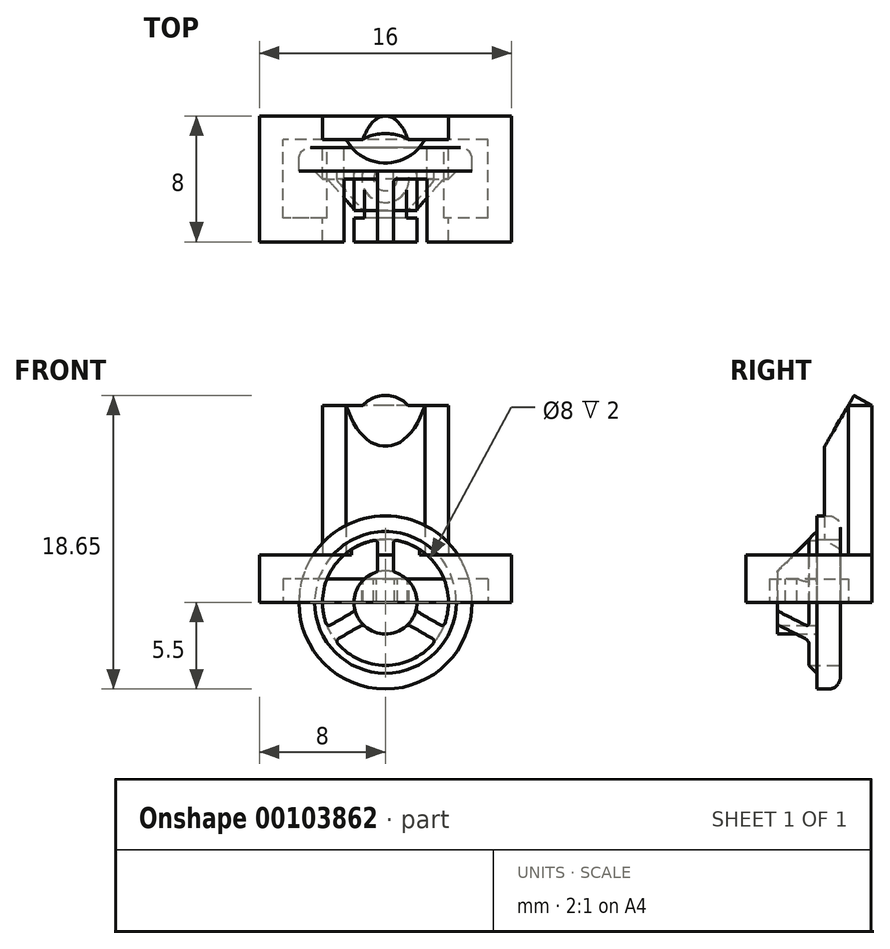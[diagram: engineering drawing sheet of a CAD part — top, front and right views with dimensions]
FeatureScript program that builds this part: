
annotation { "Feature Type Name" : "Feature", "Feature Type Description" : "" }
export const myFeature = defineFeature(function(context is Context, id is Id, definition is map)
    precondition{}
    {
        {
            var Q0;
            Q0=qCreatedBy(makeId("Top.planeOp"),FACE);
            var sketch = newSketch(context, id + "F0", { "sketchPlane" : qUnion([Q0])});
            skLineSegment(sketch, "E0.bottom", {"start": v(8, -4) * mm, "end": v(-8, -4) * mm});
            skLineSegment(sketch, "E0.top", {"start": v(8, 4) * mm, "end": v(-8, 4) * mm});
            skLineSegment(sketch, "E0.left", {"start": v(8, -4) * mm, "end": v(8, 4) * mm});
            skLineSegment(sketch, "E0.right", {"start": v(-8, -4) * mm, "end": v(-8, 4) * mm});
            skPoint(sketch, "E0.middle", {"position": v(0, 0) * mm});
            skSolve(sketch);
        }
        {
            var Q0;
            Q0=makeQuery(id+"F0.imprint","IMPRINT",FACE,{"disambiguationData":[TD([[makeQuery(id+"F0.imprint","IMPRINT",EDGE,{"derivedFrom":sQuery(id+"F0.wireOp",EDGE,"E0.bottom")}),-1.0]])]});
            extrude(context, id + "F1", {"entities" : qUnion([Q0]), "depth" : 3 * mm});
        }
        {
            var Q0;
            Q0=makeQuery(id+"F1.opExtrude","CAP_FACE",FACE,{"disambiguationData":[OSD([sQuery(id+"F0.wireOp",EDGE,"E0.bottom"),sQuery(id+"F0.wireOp",EDGE,"E0.top"),sQuery(id+"F0.wireOp",EDGE,"E0.left"),sQuery(id+"F0.wireOp",EDGE,"E0.right")])],"isStart":true});
            shell(context, id + "F2", {"entities" : qUnion([Q0]), "thickness" : 1.5 * mm});
        }
        {
            var Q0;
            Q0=makeQuery(id+"F2.opShell","OFFSET_FACE",FACE,{"disambiguationData":[OSD([sQuery(id+"F0.wireOp",EDGE,"E0.bottom"),sQuery(id+"F0.wireOp",EDGE,"E0.top"),sQuery(id+"F0.wireOp",EDGE,"E0.left"),sQuery(id+"F0.wireOp",EDGE,"E0.right")])]});
            var sketch = newSketch(context, id + "F3", { "sketchPlane" : qUnion([Q0])});
            skCircle(sketch, "E1", {"center": v(0, 0) * mm, "radius": 1.5 * mm});
            skCircle(sketch, "E2.0", {"center": v(0, 0) * mm, "radius": 0.75 * mm});
            skSolve(sketch);
        }
        {
            var Q0;
            Q0=makeQuery(id+"F3.imprint","IMPRINT",FACE,{"disambiguationData":[TD([[makeQuery(id+"F3.imprint","IMPRINT",EDGE,{"derivedFrom":sQuery(id+"F3.wireOp",EDGE,"E1")}),1.0]])]});
            var Q1;
            Q1=makeQuery(id+"F1.opExtrude","CAP_FACE",FACE,{"disambiguationData":[OSD([sQuery(id+"F0.wireOp",EDGE,"E0.bottom"),sQuery(id+"F0.wireOp",EDGE,"E0.top"),sQuery(id+"F0.wireOp",EDGE,"E0.left"),sQuery(id+"F0.wireOp",EDGE,"E0.right")])],"isStart":true});
            extrude(context, id + "F4", {"entities" : qUnion([Q0]), "operationType" : NewBodyOperationType.ADD, "endBound" : BoundingType.UP_TO_SURFACE, "endBoundEntityFace" : qUnion([Q1]), "depth" : 25 * mm});
        }
        {
            var Q0;
            Q0=makeQuery(id+"F1.opExtrude","CAP_FACE",FACE,{"disambiguationData":[OSD([sQuery(id+"F0.wireOp",EDGE,"E0.bottom"),sQuery(id+"F0.wireOp",EDGE,"E0.top"),sQuery(id+"F0.wireOp",EDGE,"E0.left"),sQuery(id+"F0.wireOp",EDGE,"E0.right")])],"isStart":false});
            var sketch = newSketch(context, id + "F5", { "sketchPlane" : qUnion([Q0])});
            skLineSegment(sketch, "E3", {"start": v(0, 4) * mm, "end": v(0, -4) * mm, "construction": true});
            skLineSegment(sketch, "E4.bottom", {"start": v(-4, 4) * mm, "end": v(4, 4) * mm});
            skLineSegment(sketch, "E4.top", {"start": v(-4, 2.5) * mm, "end": v(-2.5, 2.5) * mm});
            skLineSegment(sketch, "E4.left", {"start": v(-4, 4) * mm, "end": v(-4, 2.5) * mm});
            skLineSegment(sketch, "E4.right", {"start": v(4, 4) * mm, "end": v(4, 2.5) * mm});
            skArc(sketch, "E5", {"start": v(-2.5, 2.5) * mm, "mid": v(0, 1) * mm, "end": v(2.5, 2.5) * mm});
            skLineSegment(sketch, "E6.0", {"start": v(-4, 1) * mm, "end": v(4, 1) * mm, "construction": true});
            skLineSegment(sketch, "E7.trimOffspring", {"start": v(2.5, 2.5) * mm, "end": v(4, 2.5) * mm});
            skSolve(sketch);
        }
        {
            var Q0;
            Q0=makeQuery(id+"F5.imprint","IMPRINT",FACE,{"disambiguationData":[TD([[makeQuery(id+"F5.imprint","IMPRINT",EDGE,{"derivedFrom":sQuery(id+"F5.wireOp",EDGE,"E4.bottom")}),1.0]])]});
            extrude(context, id + "F6", {"entities" : qUnion([Q0]), "operationType" : NewBodyOperationType.ADD, "depth" : 9.5 * mm});
        }
        {
            var Q0;
            Q0=makeQuery(id+"F6.opExtrude","SWEPT_FACE",FACE,{"disambiguationData":[OSD([sQuery(id+"F5.wireOp",EDGE,"E4.left")])]});
            var sketch = newSketch(context, id + "F7", { "sketchPlane" : qUnion([Q0])});
            skLineSegment(sketch, "E8", {"start": v(-2.5, 12.5) * mm, "end": v(0.42, 12.5) * mm});
            skLineSegment(sketch, "E9", {"start": v(0.42, 12.5) * mm, "end": v(0.42, 7.44) * mm});
            skLineSegment(sketch, "E10", {"start": v(0.42, 7.44) * mm, "end": v(-2.5, 12.5) * mm});
            skSolve(sketch);
        }
        {
            var Q0;
            Q0=makeQuery(id+"F7.imprint","IMPRINT",FACE,{"disambiguationData":[TD([[makeQuery(id+"F7.imprint","IMPRINT",EDGE,{"derivedFrom":sQuery(id+"F7.wireOp",EDGE,"E8")}),-1.0]])]});
            extrude(context, id + "F8", {"entities" : qUnion([Q0]), "operationType" : NewBodyOperationType.REMOVE, "endBound" : BoundingType.THROUGH_ALL, "oppositeDirection" : true, "depth" : 25 * mm});
        }
        {
            var Q0;
            Q0=qCreatedBy(makeId("Right.planeOp"),FACE);
            var sketch = newSketch(context, id + "F9", { "sketchPlane" : qUnion([Q0])});
            skLineSegment(sketch, "E11", {"start": v(-2, 0) * mm, "end": v(-2, 2) * mm});
            skLineSegment(sketch, "E12", {"start": v(-2, 2) * mm, "end": v(0.5, 4.5) * mm});
            skLineSegment(sketch, "E13", {"start": v(0.5, 4.5) * mm, "end": v(0.5, 5.5) * mm});
            skLineSegment(sketch, "E14", {"start": v(0.5, 5.5) * mm, "end": v(2, 5.5) * mm});
            skLineSegment(sketch, "E15", {"start": v(2, 0) * mm, "end": v(-2, 0) * mm});
            skPoint(sketch, "E16.orphan", {"position": v(2.44, 0) * mm});
            skLineSegment(sketch, "E17", {"start": v(2, 5.5) * mm, "end": v(2, 0) * mm});
            skSolve(sketch);
        }
        {
            var Q0;
            Q0 = qSketchRegion(id + "F9", true);
            var Q1;
            Q1=sQuery(id+"F9.wireOp",EDGE,"E15");
            revolve(context, id + "F10", {"entities" : qUnion([Q0]), "axis" : qUnion([Q1]), "revolveType" : RevolveType.FULL});
        }
        {
            var Q0;
            Q0=makeQuery(id+"F10.opRevolve","SWEPT_FACE",FACE,{"disambiguationData":[OSD([sQuery(id+"F9.wireOp",EDGE,"E17")])]});
            var sketch = newSketch(context, id + "F11", { "sketchPlane" : qUnion([Q0])});
            skArc(sketch, "E18", {"start": v(3.77, -1.33) * mm, "mid": v(3.46, 2) * mm, "end": v(0.74, 3.93) * mm});
            skArc(sketch, "E19", {"start": v(1.96, -0.4) * mm, "mid": v(1.73, 1) * mm, "end": v(0.64, 1.9) * mm});
            skLineSegment(sketch, "E20.0", {"start": v(0.5, 3.73) * mm, "end": v(0.5, 2.09) * mm});
            skLineSegment(sketch, "E21", {"start": v(0, 6.2) * mm, "end": v(0, -6.27) * mm, "construction": true});
            skLineSegment(sketch, "E22.1.1", {"start": v(3.48, -1.43) * mm, "end": v(2.06, -0.6) * mm});
            skLineSegment(sketch, "E23", {"start": v(0, 0) * mm, "end": v(5.88, 3.4) * mm, "construction": true});
            skPoint(sketch, "E24.visualSharp", {"position": v(0.5, 3.97) * mm});
            skArc(sketch, "E24.filletArc", {"start": v(0.74, 3.93) * mm, "mid": v(0.57, 3.89) * mm, "end": v(0.5, 3.73) * mm});
            skPoint(sketch, "E25.visualSharp", {"position": v(0.5, 1.94) * mm});
            skArc(sketch, "E25.filletArc", {"start": v(0.5, 2.09) * mm, "mid": v(0.54, 1.97) * mm, "end": v(0.64, 1.9) * mm});
            skPoint(sketch, "E26.visualSharp", {"position": v(1.93, -0.54) * mm});
            skArc(sketch, "E26.filletArc", {"start": v(1.96, -0.4) * mm, "mid": v(1.97, -0.52) * mm, "end": v(2.06, -0.6) * mm});
            skPoint(sketch, "E27.visualSharp", {"position": v(3.69, -1.55) * mm});
            skArc(sketch, "E27.filletArc", {"start": v(3.48, -1.43) * mm, "mid": v(3.65, -1.45) * mm, "end": v(3.77, -1.33) * mm});
            skArc(sketch, "E28.1.0", {"start": v(-0.74, 3.93) * mm, "mid": v(-3.46, 2) * mm, "end": v(-3.77, -1.33) * mm});
            skArc(sketch, "E28.1.1", {"start": v(-3.77, -1.33) * mm, "mid": v(-3.65, -1.45) * mm, "end": v(-3.48, -1.43) * mm});
            skArc(sketch, "E28.1.2", {"start": v(-2.06, -0.6) * mm, "mid": v(-1.97, -0.52) * mm, "end": v(-1.96, -0.4) * mm});
            skArc(sketch, "E28.1.3", {"start": v(-0.64, 1.9) * mm, "mid": v(-1.73, 1) * mm, "end": v(-1.96, -0.4) * mm});
            skLineSegment(sketch, "E28.1.4", {"start": v(-3.48, -1.43) * mm, "end": v(-2.06, -0.6) * mm});
            skArc(sketch, "E28.1.5", {"start": v(-0.5, 3.73) * mm, "mid": v(-0.57, 3.89) * mm, "end": v(-0.74, 3.93) * mm});
            skLineSegment(sketch, "E28.1.6", {"start": v(-0.5, 3.73) * mm, "end": v(-0.5, 2.09) * mm});
            skArc(sketch, "E28.1.7", {"start": v(-0.64, 1.9) * mm, "mid": v(-0.54, 1.97) * mm, "end": v(-0.5, 2.09) * mm});
            skArc(sketch, "E28.2.0", {"start": v(-3.04, -2.6) * mm, "mid": v(0, -4) * mm, "end": v(3.04, -2.6) * mm});
            skArc(sketch, "E28.2.1", {"start": v(3.04, -2.6) * mm, "mid": v(3.08, -2.44) * mm, "end": v(2.98, -2.3) * mm});
            skArc(sketch, "E28.2.2", {"start": v(1.56, -1.48) * mm, "mid": v(1.44, -1.45) * mm, "end": v(1.32, -1.5) * mm});
            skArc(sketch, "E28.2.3", {"start": v(-1.32, -1.5) * mm, "mid": v(0, -2) * mm, "end": v(1.32, -1.5) * mm});
            skLineSegment(sketch, "E28.2.4", {"start": v(2.98, -2.3) * mm, "end": v(1.56, -1.48) * mm});
            skArc(sketch, "E28.2.5", {"start": v(-2.98, -2.3) * mm, "mid": v(-3.08, -2.44) * mm, "end": v(-3.04, -2.6) * mm});
            skLineSegment(sketch, "E28.2.6", {"start": v(-2.98, -2.3) * mm, "end": v(-1.56, -1.48) * mm});
            skArc(sketch, "E28.2.7", {"start": v(-1.32, -1.5) * mm, "mid": v(-1.44, -1.45) * mm, "end": v(-1.56, -1.48) * mm});
            skCircle(sketch, "E29", {"center": v(0, 0) * mm, "radius": 4 * mm});
            skSolve(sketch);
        }
        {
            var Q0;
            {var subQ0=sQuery(id+"F11.wireOp",EDGE,"E28.1.1");Q0=makeQuery(id+"F11.imprint","IMPRINT",FACE,{"disambiguationData":[TD([[makeQuery(id+"F11.imprint","IMPRINT",EDGE,{"derivedFrom":subQ0}),1.0]])]});}
            var Q1;
            Q1=makeQuery(id+"F11.imprint","IMPRINT",FACE,{"disambiguationData":[TD([[makeQuery(id+"F11.imprint","IMPRINT",EDGE,{"derivedFrom":sQuery(id+"F11.wireOp",EDGE,"E19")}),-1.0]])]});
            var Q2;
            {var subQ0=sQuery(id+"F11.wireOp",EDGE,"E28.2.1");Q2=makeQuery(id+"F11.imprint","IMPRINT",FACE,{"disambiguationData":[TD([[makeQuery(id+"F11.imprint","IMPRINT",EDGE,{"derivedFrom":subQ0}),1.0]])]});}
            extrude(context, id + "F12", {"entities" : qUnion([Q0, Q1, Q2]), "operationType" : NewBodyOperationType.REMOVE, "endBound" : BoundingType.THROUGH_ALL, "oppositeDirection" : true, "depth" : 25 * mm});
        }
        {
            var Q0;
            Q0=makeQuery(id+"F11.imprint","IMPRINT",FACE,{"disambiguationData":[TD([[makeQuery(id+"F11.imprint","IMPRINT",EDGE,{"derivedFrom":sQuery(id+"F11.wireOp",EDGE,"E19")}),1.0]])]});
            extrude(context, id + "F13", {"entities" : qUnion([Q0]), "operationType" : NewBodyOperationType.REMOVE, "oppositeDirection" : true, "depth" : 1.5 * mm});
        }
        {
            var Q0;
            {var subQ0=sQuery(id+"F11.wireOp",EDGE,"E29");var subQ1=makeQuery(id+"F11.imprint","INTERSECT",VERTEX,{"derivedFrom":[sQuery(id+"F11.wireOp",EDGE,"E27.filletArc"),subQ0]});var subQ2=makeQuery(id+"F11.imprint","INTERSECT",VERTEX,{"derivedFrom":[sQuery(id+"F11.wireOp",EDGE,"E28.2.1"),subQ0]});var subQ3=makeQuery(id+"F11.imprint","INTERSECT",VERTEX,{"derivedFrom":[sQuery(id+"F11.wireOp",EDGE,"E28.1.1"),subQ0]});var subQ5=makeQuery(id+"F11.imprint","INTERSECT",VERTEX,{"derivedFrom":[sQuery(id+"F11.wireOp",EDGE,"E24.filletArc"),subQ0]});Q0=makeQuery(id+"F13.boolean.opBoolean","MERGE",EDGE,{"derivedFrom":[makeQuery(id+"F12.boolean.opBoolean","COPY",EDGE,{"derivedFrom":makeQuery(id+"F12.opExtrude","CAP_EDGE",EDGE,{"disambiguationData":[OSD([subQ0]),TDD([makeQuery(id+"F11.imprint","IMPRINT",EDGE,{"disambiguationData":[TD([[subQ3,1.0]])],"derivedFrom":subQ0})])],"isStart":true})}),makeQuery(id+"F12.boolean.opBoolean","COPY",EDGE,{"derivedFrom":makeQuery(id+"F12.opExtrude","CAP_EDGE",EDGE,{"disambiguationData":[OSD([subQ0]),TDD([makeQuery(id+"F11.imprint","IMPRINT",EDGE,{"disambiguationData":[TD([[subQ2,1.0]])],"derivedFrom":subQ0})])],"isStart":true})}),makeQuery(id+"F12.boolean.opBoolean","COPY",EDGE,{"derivedFrom":makeQuery(id+"F12.opExtrude","CAP_EDGE",EDGE,{"disambiguationData":[OSD([subQ0]),TDD([makeQuery(id+"F11.imprint","IMPRINT",EDGE,{"disambiguationData":[TD([[subQ5,1.0]])],"derivedFrom":subQ0})])],"isStart":true})}),makeQuery(id+"F13.opExtrude","CAP_EDGE",EDGE,{"disambiguationData":[OSD([subQ0]),TDD([makeQuery(id+"F11.imprint","IMPRINT",EDGE,{"disambiguationData":[TD([[subQ5,-1.0]])],"derivedFrom":subQ0})])],"isStart":true}),makeQuery(id+"F13.opExtrude","CAP_EDGE",EDGE,{"disambiguationData":[OSD([subQ0]),TDD([makeQuery(id+"F11.imprint","IMPRINT",EDGE,{"disambiguationData":[TD([[subQ3,-1.0]])],"derivedFrom":subQ0})])],"isStart":true}),makeQuery(id+"F13.opExtrude","CAP_EDGE",EDGE,{"disambiguationData":[OSD([subQ0]),TDD([makeQuery(id+"F11.imprint","IMPRINT",EDGE,{"disambiguationData":[TD([[subQ1,1.0]])],"derivedFrom":subQ0})])],"isStart":true})]});}
            var Q1;
            Q1=makeQuery(id+"F10.opRevolve","SWEPT_EDGE",EDGE,{"disambiguationData":[OSD([sQuery(id+"F9.wireOp",EDGE,"E14"),sQuery(id+"F9.wireOp",EDGE,"E17")])]});
            fillet(context, id + "F14", {"entities" : qUnion([Q0, Q1]), "radius" : .75 * mm, "tangentPropagation" : true, "allowEdgeOverflow" : false});
        }
        {
            var Q0;
            Q0=makeQuery(id+"F8.boolean.opBoolean","COPY",FACE,{"derivedFrom":makeQuery(id+"F8.opExtrude","SWEPT_FACE",FACE,{"disambiguationData":[OSD([sQuery(id+"F7.wireOp",EDGE,"E10")])]})});
            var sketch = newSketch(context, id + "F15", { "sketchPlane" : qUnion([Q0])});
            skCircle(sketch, "E30", {"center": v(0, 11.08) * mm, "radius": 1.75 * mm});
            skLineSegment(sketch, "E31", {"start": v(0, 12.08) * mm, "end": v(0, 9.08) * mm, "construction": true});
            skSolve(sketch);
        }
        {
            var Q0;
            {var subQ0=sQuery(id+"F15.wireOp",EDGE,"E30");var subQ1=makeQuery(id+"F8.boolean.opBoolean","COPY",EDGE,{"derivedFrom":makeQuery(id+"F8.opExtrude","SWEPT_EDGE",EDGE,{"disambiguationData":[OSD([sQuery(id+"F5.wireOp",EDGE,"E4.top"),sQuery(id+"F5.wireOp",EDGE,"E4.left"),sQuery(id+"F7.wireOp",EDGE,"E8"),sQuery(id+"F7.wireOp",EDGE,"E10")])]})});var subQ2=makeQuery(id+"F15.imprint","INTERSECT",VERTEX,{"disambiguationData":[OD(0.0)],"derivedFrom":[subQ1,subQ0]});Q0=makeQuery(id+"F15.imprint","IMPRINT",FACE,{"disambiguationData":[TD([[makeQuery(id+"F15.imprint","IMPRINT",EDGE,{"disambiguationData":[TD([[subQ2,1.0]])],"derivedFrom":subQ0}),1.0]])]});}
            extrude(context, id + "F16", {"entities" : qUnion([Q0]), "operationType" : NewBodyOperationType.ADD, "endBound" : BoundingType.UP_TO_NEXT, "oppositeDirection" : true, "depth" : 25 * mm});
        }
    });
